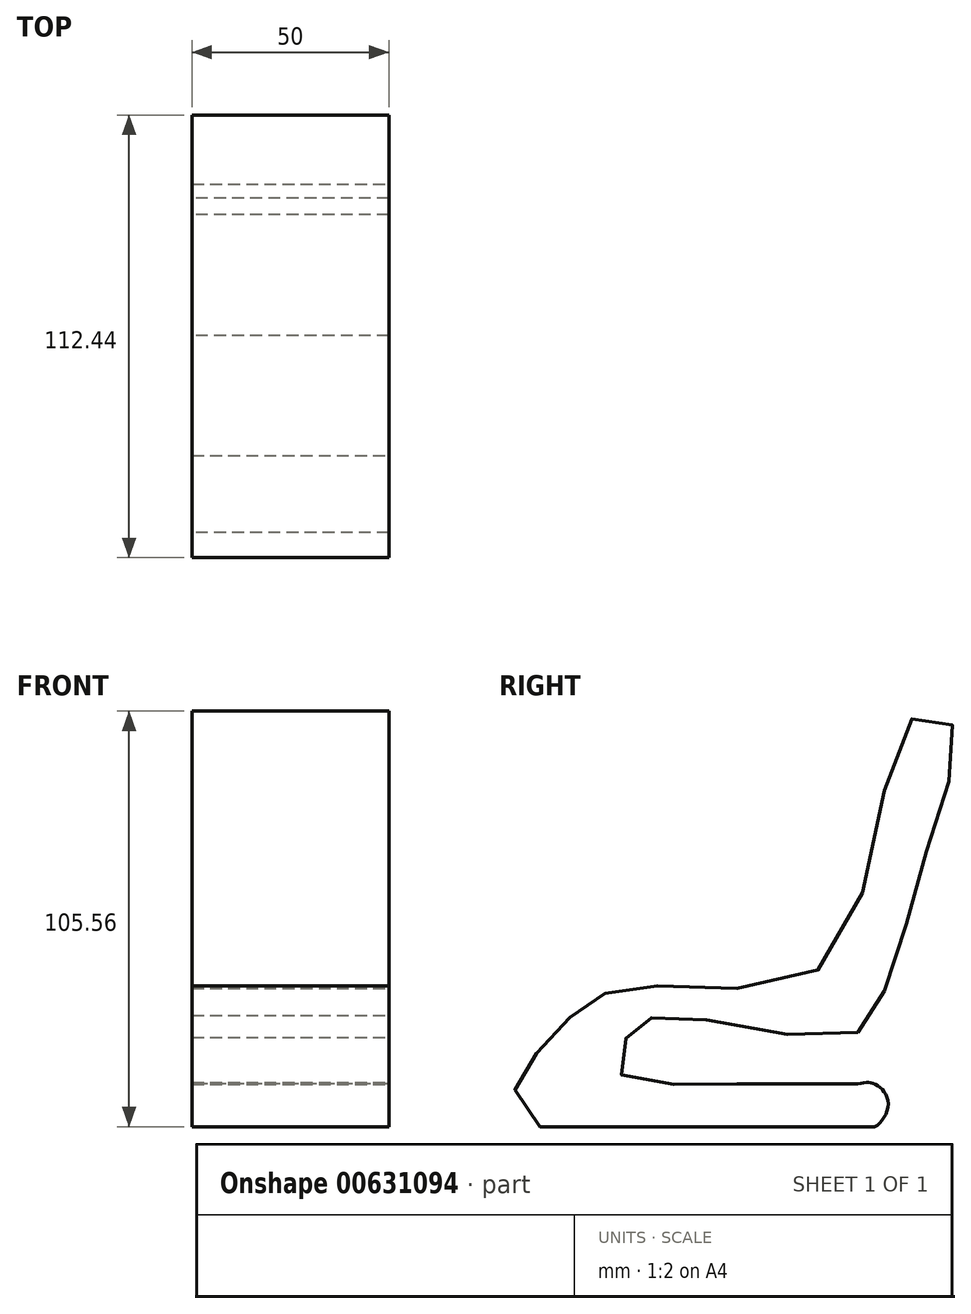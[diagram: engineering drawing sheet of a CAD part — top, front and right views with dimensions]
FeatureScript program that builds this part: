
annotation { "Feature Type Name" : "Feature", "Feature Type Description" : "" }
export const myFeature = defineFeature(function(context is Context, id is Id, definition is map)
    precondition{}
    {
        {
            var Q0;
            Q0=qCreatedBy(makeId("Right.planeOp"),FACE);
            var sketch = newSketch(context, id + "F0", { "sketchPlane" : qUnion([Q0])});
            skLineSegment(sketch, "E0", {"start": v(-50.1, -56.53) * mm, "end": v(34.9, -56.53) * mm});
            skLineSegment(sketch, "E1", {"start": v(0, -45.65) * mm, "end": v(30.68, -45.65) * mm});
            skFitSpline(sketch, "E2", {"points": [v(30.68, -45.65) * mm, v(34.9, -45.65) * mm, v(38.35, -50.16) * mm, v(34.9, -56.53) * mm], "startDerivative": vector(18.85, 4.4) * mm, "endDerivative": vector(-16.54, -6.9) * mm});
            skFitSpline(sketch, "E3", {"points": [v(-50.1, -56.53) * mm, v(-56.4, -48.3) * mm, v(-53.74, -41.4) * mm, v(-46.04, -32.38) * mm, v(-38.61, -25.48) * mm, v(-30.65, -21.76) * mm, v(-11.54, -20.97) * mm, v(21.63, -15.93) * mm, v(36.98, 26.8) * mm, v(47.1, 48.83) * mm, v(55.33, 44.31) * mm, v(51.88, 25.74) * mm, v(44.45, 0) * mm, v(36.98, -23.36) * mm, v(30.39, -32.64) * mm, v(2.52, -31.32) * mm, v(-19.24, -28.4) * mm, v(-25.6, -30.79) * mm, v(-28.8, -35.03) * mm, v(-30.12, -42.46) * mm, v(-19.24, -45.65) * mm, v(0, -45.65) * mm], "startDerivative": vector(-204.7, 102.44) * mm, "endDerivative": vector(366.82, 6.86) * mm});
            skSolve(sketch);
        }
        {
            var Q0;
            Q0=makeQuery(id+"F0.imprint","IMPRINT",FACE,{"disambiguationData":[TD([[makeQuery(id+"F0.imprint","IMPRINT",EDGE,{"derivedFrom":sQuery(id+"F0.wireOp",EDGE,"E0")}),1.0]])]});
            extrude(context, id + "F1", {"entities" : qUnion([Q0]), "depth" : 50 * mm, "offsetDistance" : 25 * mm});
        }
    });
